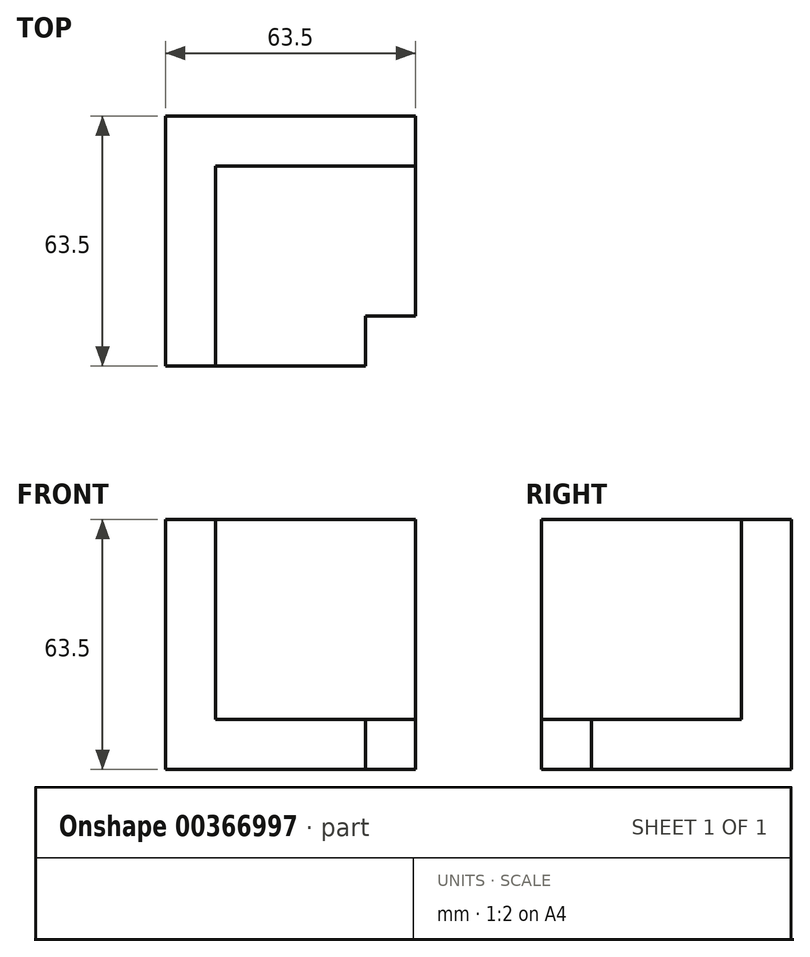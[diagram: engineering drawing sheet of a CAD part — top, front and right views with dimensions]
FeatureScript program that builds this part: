
annotation { "Feature Type Name" : "Feature", "Feature Type Description" : "" }
export const myFeature = defineFeature(function(context is Context, id is Id, definition is map)
    precondition{}
    {
        {
            var Q0;
            Q0=qCreatedBy(makeId("Top.planeOp"),FACE);
            var sketch = newSketch(context, id + "F0", { "sketchPlane" : qUnion([Q0])});
            skLineSegment(sketch, "E0.bottom", {"start": v(0, 0) * mm, "end": v(12.7, 0) * mm});
            skLineSegment(sketch, "E0.top", {"start": v(0, -63.5) * mm, "end": v(12.7, -63.5) * mm});
            skLineSegment(sketch, "E0.left", {"start": v(0, 0) * mm, "end": v(0, -63.5) * mm});
            skLineSegment(sketch, "E0.right", {"start": v(12.7, 0) * mm, "end": v(12.7, -63.5) * mm});
            skSolve(sketch);
        }
        {
            var Q0;
            Q0 = qSketchRegion(id + "F0", true);
            extrude(context, id + "F1", {"entities" : qUnion([Q0]), "depth" : 63.5 * mm});
        }
        {
            var Q0;
            Q0=makeQuery(id+"F1.opExtrude","SWEPT_FACE",FACE,{"disambiguationData":[OSD([sQuery(id+"F0.wireOp",EDGE,"E0.right")])]});
            var sketch = newSketch(context, id + "F2", { "sketchPlane" : qUnion([Q0])});
            skLineSegment(sketch, "E1.bottom", {"start": v(0, 0) * mm, "end": v(-12.7, 0) * mm});
            skLineSegment(sketch, "E1.top", {"start": v(0, 63.5) * mm, "end": v(-12.7, 63.5) * mm});
            skLineSegment(sketch, "E1.left", {"start": v(0, 0) * mm, "end": v(0, 63.5) * mm});
            skLineSegment(sketch, "E1.right", {"start": v(-12.7, 0) * mm, "end": v(-12.7, 63.5) * mm});
            skSolve(sketch);
        }
        {
            var Q0;
            Q0 = qSketchRegion(id + "F2", true);
            extrude(context, id + "F3", {"entities" : qUnion([Q0]), "operationType" : NewBodyOperationType.ADD, "depth" : 50.8 * mm});
        }
        {
            var Q0;
            Q0=qCreatedBy(makeId("Front.planeOp"),FACE);
            var sketch = newSketch(context, id + "F4", { "sketchPlane" : qUnion([Q0])});
            skLineSegment(sketch, "E2.bottom", {"start": v(0, 0) * mm, "end": v(50.8, 0) * mm});
            skLineSegment(sketch, "E2.top", {"start": v(0, 12.7) * mm, "end": v(50.8, 12.7) * mm});
            skLineSegment(sketch, "E2.left", {"start": v(0, 0) * mm, "end": v(0, 12.7) * mm});
            skLineSegment(sketch, "E2.right", {"start": v(50.8, 0) * mm, "end": v(50.8, 12.7) * mm});
            skSolve(sketch);
        }
        {
            var Q0;
            Q0 = qSketchRegion(id + "F4", true);
            extrude(context, id + "F5", {"entities" : qUnion([Q0]), "operationType" : NewBodyOperationType.ADD, "depth" : 63.5 * mm});
        }
        {
            var Q0;
            Q0=makeQuery(id+"F3.opExtrude","SWEPT_FACE",FACE,{"disambiguationData":[OSD([sQuery(id+"F2.wireOp",EDGE,"E1.right")])]});
            var sketch = newSketch(context, id + "F6", { "sketchPlane" : qUnion([Q0])});
            skLineSegment(sketch, "E3.bottom", {"start": v(63.5, 0) * mm, "end": v(50.8, 0) * mm});
            skLineSegment(sketch, "E3.top", {"start": v(63.5, 12.7) * mm, "end": v(50.8, 12.7) * mm});
            skLineSegment(sketch, "E3.left", {"start": v(63.5, 0) * mm, "end": v(63.5, 12.7) * mm});
            skLineSegment(sketch, "E3.right", {"start": v(50.8, 0) * mm, "end": v(50.8, 12.7) * mm});
            skSolve(sketch);
        }
        {
            var Q0;
            Q0 = qSketchRegion(id + "F6", true);
            extrude(context, id + "F7", {"entities" : qUnion([Q0]), "operationType" : NewBodyOperationType.ADD, "depth" : 38.1 * mm});
        }
    });
